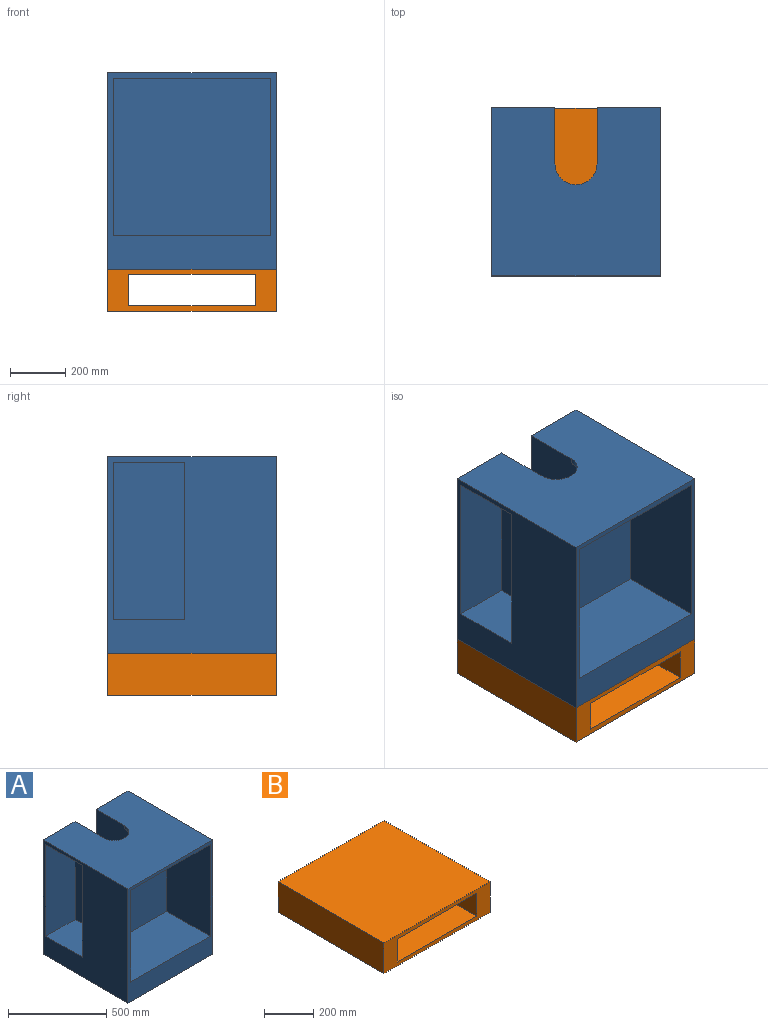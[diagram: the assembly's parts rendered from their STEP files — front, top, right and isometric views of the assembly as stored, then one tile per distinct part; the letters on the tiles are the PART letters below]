
ASSEMBLY  parts=2 mates=1
PART A: 35 faces, bbox 609.6x609.6x711.2 mm
  f0: plane 590.55x571.5mm, normal (0,0,-1), area 297410.9mm2, adj f5,f8,f12,f14,f29,f31,f32,f33
  f1: plane 571.5x311.15mm, normal (0,0,-1), area 177822.2mm2, adj f10,f22,f23,f24
  f2: plane 260.35x209.55mm, normal (0,0,-1), area 54556.3mm2, adj f11,f19,f20,f21
  f3: plane 76.2x76.2mm, normal (0,0,-1), area 1246.1mm2, adj f13,f14,f18
  f4: plane 76.2x76.2mm, normal (0,0,-1), area 1246.1mm2, adj f12,f13,f18
  f5: plane 711.2x228.6mm, normal (0,1,0), area 141290mm2, adj f0,f6,f11,f14,f33,f34
  f6: plane 609.6x609.6mm, normal (0,0,1), area 331523.7mm2, adj f5,f8,f9,f10,f11,f12,f13,f14
  f7: plane 260.35x209.55mm, normal (0,0,-1), area 54556.3mm2, adj f9,f15,f16,f17
  f8: plane 711.2x228.6mm, normal (0,1,0), area 141290mm2, adj f0,f6,f9,f12,f31,f34
  f9: plane 711.2x609.6mm, normal (-1,0,0), area 284757.5mm2, adj f6,f7,f8,f10,f15,f17,f25,f34
  f10: plane 711.2x609.6mm, normal (0,-1,0), area 106935.3mm2, adj f1,f6,f9,f11,f22,f24,f30,f34
  f11: plane 711.2x609.6mm, normal (1,0,0), area 284757.5mm2, adj f2,f5,f6,f10,f19,f21,f28,f34
  f12: plane 609.6x279.4mm, normal (1,0,0), area 167419mm2, adj f0,f4,f6,f8,f13,f18,f26,f29
  f13: cylinder r=76.2mm len=152.4mm, axis (0,0,1), area 4560.4mm2, adj f3,f4,f6,f12,f14
  f14: plane 609.6x279.4mm, normal (-1,0,0), area 167419mm2, adj f0,f3,f5,f6,f13,f18,f27,f29
  f15: plane 571.5x209.55mm, normal (0,1,0), area 119757.8mm2, adj f7,f9,f16,f25
  f16: plane 571.5x260.35mm, normal (-1,0,0), area 148790mm2, adj f7,f15,f17,f25
  f17: plane 571.5x209.55mm, normal (0,-1,0), area 119757.8mm2, adj f7,f9,f16,f25
  f18: plane 571.5x152.4mm, normal (0,1,0), area 87096.6mm2, adj f3,f4,f12,f14,f26,f27
  f19: plane 571.5x209.55mm, normal (0,-1,0), area 119757.8mm2, adj f2,f11,f20,f28
  f20: plane 571.5x260.35mm, normal (1,0,0), area 148790mm2, adj f2,f19,f21,f28
  f21: plane 571.5x209.55mm, normal (0,1,0), area 119757.8mm2, adj f2,f11,f20,f28
  f22: plane 571.5x311.15mm, normal (-1,0,0), area 177822.2mm2, adj f1,f10,f23,f30
  f23: plane 571.5x571.5mm, normal (0,-1,0), area 326612.2mm2, adj f1,f22,f24,f30
  f24: plane 571.5x311.15mm, normal (1,0,0), area 177822.2mm2, adj f1,f10,f23,f30
  f25: plane 260.35x209.55mm, normal (0,0,1), area 54556.3mm2, adj f9,f15,f16,f17
  f26: plane 76.2x76.2mm, normal (0,0,1), area 1246.1mm2, adj f12,f18,f29
  f27: plane 76.2x76.2mm, normal (0,0,1), area 1246.1mm2, adj f14,f18,f29
  f28: plane 260.35x209.55mm, normal (0,0,1), area 54556.3mm2, adj f11,f19,f20,f21
  f29: cylinder r=76.2mm len=152.4mm, axis (0,0,1), area 4560.4mm2, adj f0,f12,f14,f26,f27
  f30: plane 571.5x311.15mm, normal (0,0,1), area 177822.2mm2, adj f10,f22,f23,f24
  f31: plane 590.55x101.6mm, normal (1,0,0), area 59999.9mm2, adj f0,f8,f32,f34
  f32: plane 571.5x101.6mm, normal (0,1,0), area 58064.4mm2, adj f0,f31,f33,f34
  f33: plane 590.55x101.6mm, normal (-1,0,0), area 59999.9mm2, adj f0,f5,f32,f34
  f34: plane 609.6x609.6mm, normal (0,0,-1), area 34112.8mm2, adj f5,f8,f9,f10,f11,f31,f32,f33
PART B: 20 faces, bbox 609.6x609.6x152.4 mm
  f0: plane 590.55x38.1mm, normal (0,0,1), area 22500mm2, adj f2,f10,f18,f19
  f1: plane 609.6x457.2mm, normal (0,0,-1), area 278709.1mm2, adj f9,f10,f15,f17
  f2: plane 590.55x114.3mm, normal (-1,0,0), area 67499.9mm2, adj f0,f10,f11,f19
  f3: plane 590.55x38.1mm, normal (0,0,-1), area 22500mm2, adj f10,f12,f14,f16
  f4: plane 609.6x457.2mm, normal (0,0,1), area 278709.1mm2, adj f9,f10,f15,f17
  f5: plane 609.6x609.6mm, normal (0,0,1), area 371612.2mm2, adj f6,f8,f9,f10
  f6: plane 609.6x152.4mm, normal (-1,0,0), area 92903mm2, adj f5,f7,f9,f10
  f7: plane 609.6x609.6mm, normal (0,0,-1), area 371612.2mm2, adj f6,f8,f9,f10
  f8: plane 609.6x152.4mm, normal (1,0,0), area 92903mm2, adj f5,f7,f9,f10
  f9: plane 609.6x152.4mm, normal (0,-1,0), area 40645.1mm2, adj f1,f4,f5,f6,f7,f8,f15,f17
  f10: plane 609.6x152.4mm, normal (0,1,0), area 31935.4mm2, adj f0,f1,f2,f3,f4,f5,f6,f7
  f11: plane 590.55x38.1mm, normal (0,0,-1), area 22500mm2, adj f2,f10,f18,f19
  f12: plane 590.55x114.3mm, normal (1,0,0), area 67499.9mm2, adj f3,f10,f13,f14
  f13: plane 590.55x38.1mm, normal (0,0,1), area 22500mm2, adj f10,f12,f14,f16
  f14: plane 114.3x38.1mm, normal (0,1,0), area 4354.8mm2, adj f3,f12,f13,f16
  f15: plane 609.6x114.3mm, normal (1,0,0), area 69677.3mm2, adj f1,f4,f9,f10
  f16: plane 590.55x114.3mm, normal (-1,0,0), area 67499.9mm2, adj f3,f10,f13,f14
  f17: plane 609.6x114.3mm, normal (-1,0,0), area 69677.3mm2, adj f1,f4,f9,f10
  f18: plane 590.55x114.3mm, normal (1,0,0), area 67499.9mm2, adj f0,f10,f11,f19
  f19: plane 114.3x38.1mm, normal (0,1,0), area 4354.8mm2, adj f0,f2,f11,f18
PLACE A t=(0,0,777.88)mm
PLACE B at identity fixed
MATE fastened B.f5 <-> A.f34  axis (0,0,1) through (304.8,-304.8,76.2)mm
